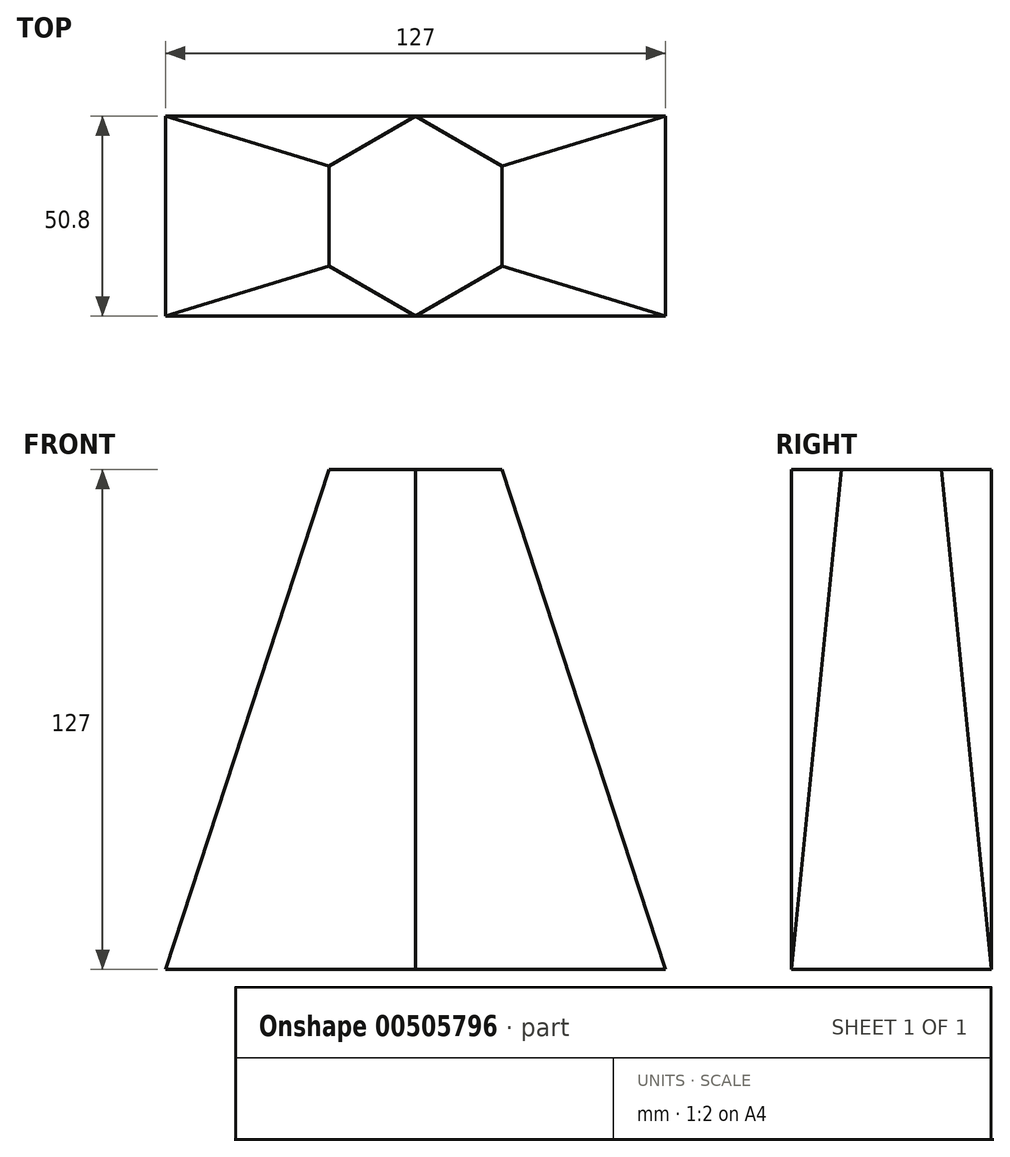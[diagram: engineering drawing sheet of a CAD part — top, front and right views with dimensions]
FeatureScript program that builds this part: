
annotation { "Feature Type Name" : "Feature", "Feature Type Description" : "" }
export const myFeature = defineFeature(function(context is Context, id is Id, definition is map)
    precondition{}
    {
        {
            var Q0;
            Q0=qCreatedBy(makeId("Top.planeOp"),FACE);
            cPlane(context, id + "F0", {"entities" : qUnion([Q0]), "cplaneType" : CPlaneType.OFFSET, "offset" : 127 * mm, "width" : 152.4 * mm, "height" : 152.4 * mm});
        }
        {
            var Q0;
            Q0=qCreatedBy(makeId("Top.planeOp"),FACE);
            var sketch = newSketch(context, id + "F1", { "sketchPlane" : qUnion([Q0])});
            skLineSegment(sketch, "E0.bottom", {"start": v(-63.5, 25.4) * mm, "end": v(63.5, 25.4) * mm});
            skLineSegment(sketch, "E0.top", {"start": v(-63.5, -25.4) * mm, "end": v(63.5, -25.4) * mm});
            skLineSegment(sketch, "E0.left", {"start": v(-63.5, 25.4) * mm, "end": v(-63.5, -25.4) * mm});
            skLineSegment(sketch, "E0.right", {"start": v(63.5, 25.4) * mm, "end": v(63.5, -25.4) * mm});
            skPoint(sketch, "E0.middle", {"position": v(0, 0) * mm});
            skSolve(sketch);
        }
        {
            var Q0;
            Q0=qCreatedBy(id+"F0.planeOp",FACE);
            var sketch = newSketch(context, id + "F2", { "sketchPlane" : qUnion([Q0])});
            skCircle(sketch, "E1.cCircle", {"center": v(0, 0) * mm, "radius": 25.4 * mm, "construction": true});
            skLineSegment(sketch, "E1.0", {"start": v(0, 25.4) * mm, "end": v(22, 12.7) * mm});
            skLineSegment(sketch, "E1.1", {"start": v(22, 12.7) * mm, "end": v(22, -12.7) * mm});
            skLineSegment(sketch, "E1.2", {"start": v(22, -12.7) * mm, "end": v(0, -25.4) * mm});
            skLineSegment(sketch, "E1.3", {"start": v(0, -25.4) * mm, "end": v(-22, -12.7) * mm});
            skLineSegment(sketch, "E1.4", {"start": v(-22, -12.7) * mm, "end": v(-22, 12.7) * mm});
            skLineSegment(sketch, "E1.5", {"start": v(-22, 12.7) * mm, "end": v(0, 25.4) * mm});
            skSolve(sketch);
        }
        {
            var Q0;
            Q0=makeQuery(id+"F1.imprint","IMPRINT",FACE,{"disambiguationData":[TD([[makeQuery(id+"F1.imprint","IMPRINT",EDGE,{"derivedFrom":sQuery(id+"F1.wireOp",EDGE,"E0.bottom")}),-1.0]])]});
            var Q1;
            Q1=makeQuery(id+"F2.imprint","IMPRINT",FACE,{"disambiguationData":[TD([[makeQuery(id+"F2.imprint","IMPRINT",EDGE,{"derivedFrom":sQuery(id+"F2.wireOp",EDGE,"E1.0")}),-1.0]])]});
            loft(context, id + "F3", {"sheetProfilesArray" : [{ "sheetProfileEntities" : qUnion([Q0]) }, { "sheetProfileEntities" : qUnion([Q1]) }]});
        }
    });
